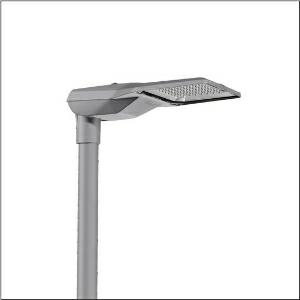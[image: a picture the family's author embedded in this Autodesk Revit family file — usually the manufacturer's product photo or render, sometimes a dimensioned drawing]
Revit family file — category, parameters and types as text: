
# Revit family: streetlight_sl_21_midi___stw1_0a_5xe3e43s08mb_fad8
name_source: partatom
category: Lighting Fixtures
units: mm (PartAtom-declared; Revit-internal decimal feet)

## family parameters
Cut with Voids When Loaded = No
Host = Face
Light Source = No
Part Type = Normal
Room Calculation Point = No
Round Connector Dimension = Use Diameter
Shared = No

## types (1)
- --- (1 x LED, 20180 lm, 147 W, 4000K)
    Apparent Load = 147 VA
    CIE Flux Codes = 38 75 98 100 100
    Color Rendering = 70
    Color Temperature = 4000K
    Default Elevation = 1800 mm
    Description = Streetlight SL 21 midi, mast luminaire, primary light control with lens, of PMMA, primary optical cover: cover, of toughened safety glass, transparent, light distribution: STW1.0a, light emission: direct distribution, primary light characteristic: asymmetric, installation type: side-entry, post-top, LED, High Power LED, rated luminous flux: 20.180lm, luminous efficacy: 137lm/W, light colour: 740, colour temperature: 4000K, control gear: D4i, control: overheat protection, constant luminous flux control, time-dependent luminous flux control, flexible luminous flux parameterisation, pre-setting: logarithmic dimming characteristic, mains connection: 230..240V, AC, 50/60Hz, start of lifetime: 147W, end of service life: 155W, reduction: 65W, luminaire housing, of diecast aluminium, powder-coated, SITECO metallic grey (DB 702S), corrosivity category C5 high according to DIN EN ISO 12944, please order mast flange separately, inclination adjustable: 0°, 5°, 10°, 15°, sealing non-destructively replaceable, multi-level sealing system, length: 644mm, width: 335mm, height: 110mm, mast flange for spigot size: 42mm (side-entry): 5XC10008XM4, 60/48mm (side-entry/post-top): 5XC10108XM2, 76/60mm (side-entry/post-top): 5XC10108XM1, mounting height: 4..8m, Smart Interface above, protection rating (complete): IP66, insulation class (complete): insulation class II (safety insulation), certification: CE, ENEC, ENEC+, VDE, impact resistance: IK10, permissible operating ambient temperature for outdoor applications: -40..+50°C, standard-compliant lighting for roads and squares, packaging unit: 1 piece

Light Distribution: STW1.0a
    Height = 111 mm
    Lamp = 1 x LED
    Lamp Light Flux = 20180 lm
    Lamp Power = 147 W
    Lamp count = 1
    Length = 644 mm
    Luminous efficacy = 137 lm/W
    Manufacturer = Siteco
    ModVariant = No
    Model = 5XE3E43S08MB
    Number of Poles = 1
    OnlyDefault = Yes
    Power Factor = 1
    Product Name = Streetlight SL 21 midi | STW1.0a
    Product group = mast luminaire | pylon top
    ProductGroupID = 6100
    Protection Class = Protection class II
    Protection Degree = IP 66
    RLX_Detail_Level = 1
    RLX_Emergency_Light_Flux = 0 lm
    RLX_Emergency_Type = 0
    RLX_Emergency_Type_DB = No
    RlxData = <blob elided: 26901 chars, md5=47aee5cf>
    Socket = socket
    Standby Power = 0 W
    System Light Flux = 20180 lm
    System Power = 147 W
    Type Comments = factory setting: luminous flux: 100 % | dim-lin: 254 | 750 mA
    Type Image = l_1004302.jpg
    URL = http://relux.com
    VarID = @adj_185411
    Voltage = 0 V
    Weight = 0.00 kg
    Width = 336 mm

## geometry (parser evidence)
native form markers: Blend x4, Sweep x13
no freeform markers — native parametric forms only
